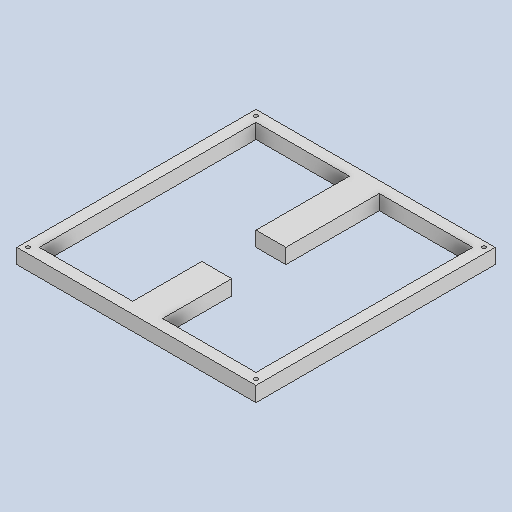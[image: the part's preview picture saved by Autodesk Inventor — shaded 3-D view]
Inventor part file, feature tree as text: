
AUTODESK INVENTOR PART (.ipt)
format: ipt  version: 2024 (Build 280153000, 153)  size: 292,352 bytes
history: native  units: in
note: dims shown in document units (in); Inventor stores cm internally (conversion verified against a paired STEP export)
features: extrude x2, projected_geometry x2
ambient origin geometry x8: Origin, YZ Plane, XZ Plane, XY Plane, X Axis, Y Axis, Z Axis, Center Point
bodies: Solid1 (feature_tree)
feature tree (4):
  extrude  "Extrusion1"  Depth=4.0in
  extrude  "Extrusion2"  Depth=4.0in
  projected_geometry  "Projected Loop1"
  projected_geometry  "Projected Loop2"
